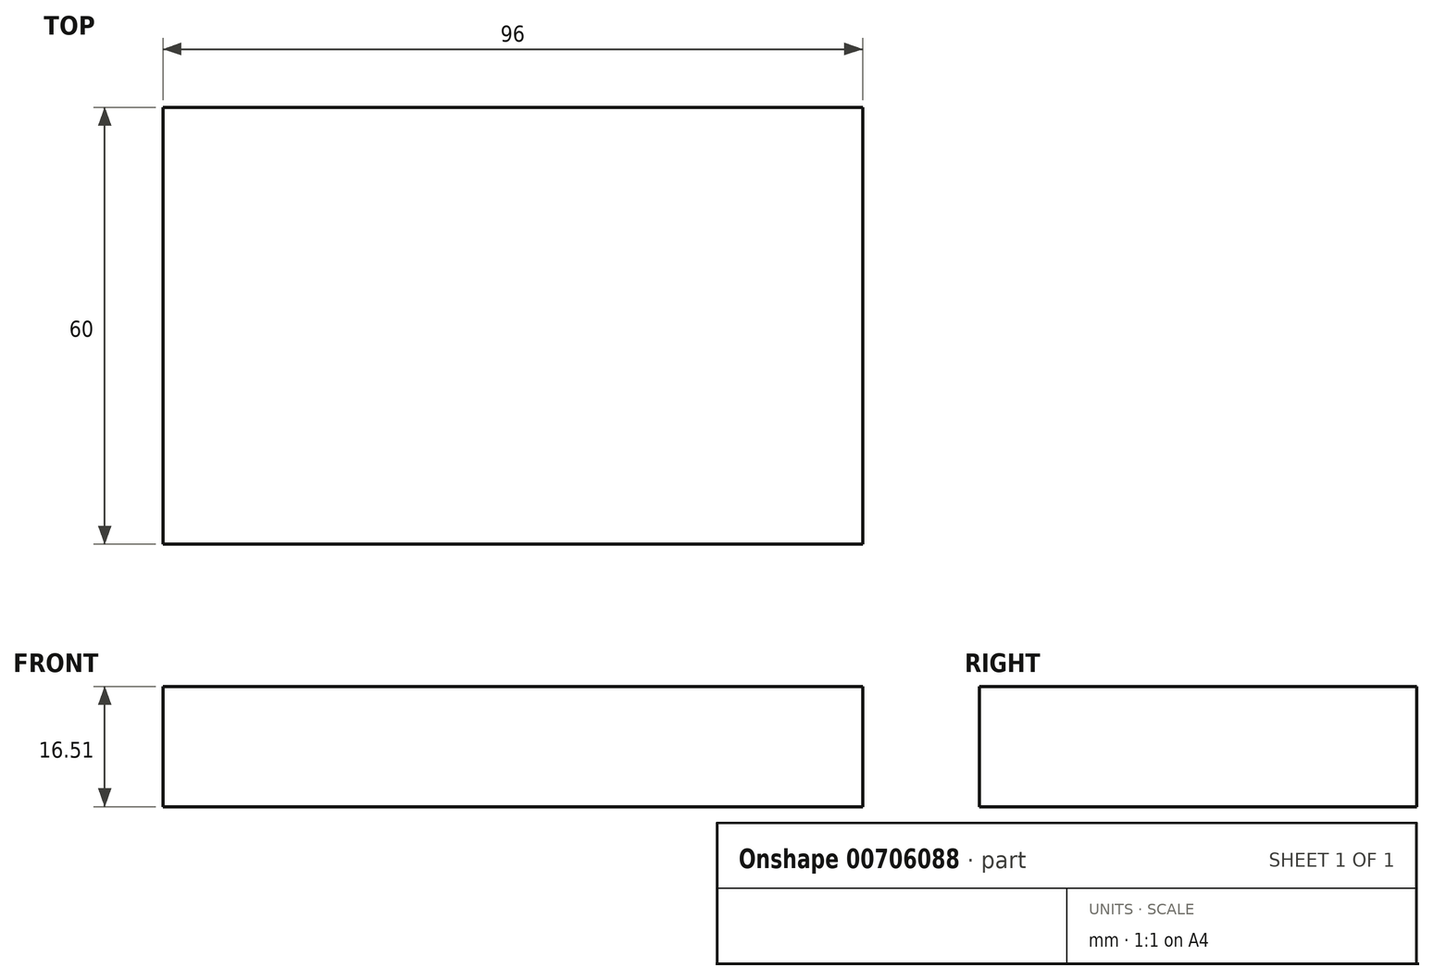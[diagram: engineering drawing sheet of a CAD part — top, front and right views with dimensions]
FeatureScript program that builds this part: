
annotation { "Feature Type Name" : "Feature", "Feature Type Description" : "" }
export const myFeature = defineFeature(function(context is Context, id is Id, definition is map)
    precondition{}
    {
        {
            var Q0;
            Q0=qCreatedBy(makeId("Top.planeOp"),FACE);
            var sketch = newSketch(context, id + "F0", { "sketchPlane" : qUnion([Q0])});
            skLineSegment(sketch, "E0.bottom", {"start": v(-48, -30) * mm, "end": v(48, -30) * mm});
            skLineSegment(sketch, "E0.top", {"start": v(-48, 30) * mm, "end": v(48, 30) * mm});
            skLineSegment(sketch, "E0.left", {"start": v(-48, -30) * mm, "end": v(-48, 30) * mm});
            skLineSegment(sketch, "E0.right", {"start": v(48, -30) * mm, "end": v(48, 30) * mm});
            skPoint(sketch, "E0.middle", {"position": v(0, 0) * mm});
            skSolve(sketch);
        }
        {
            var Q0;
            Q0 = qSketchRegion(id + "F0", true);
            extrude(context, id + "F1", {"entities" : qUnion([Q0]), "depth" : 16.5 * mm, "offsetDistance" : 25.4 * mm});
        }
    });
